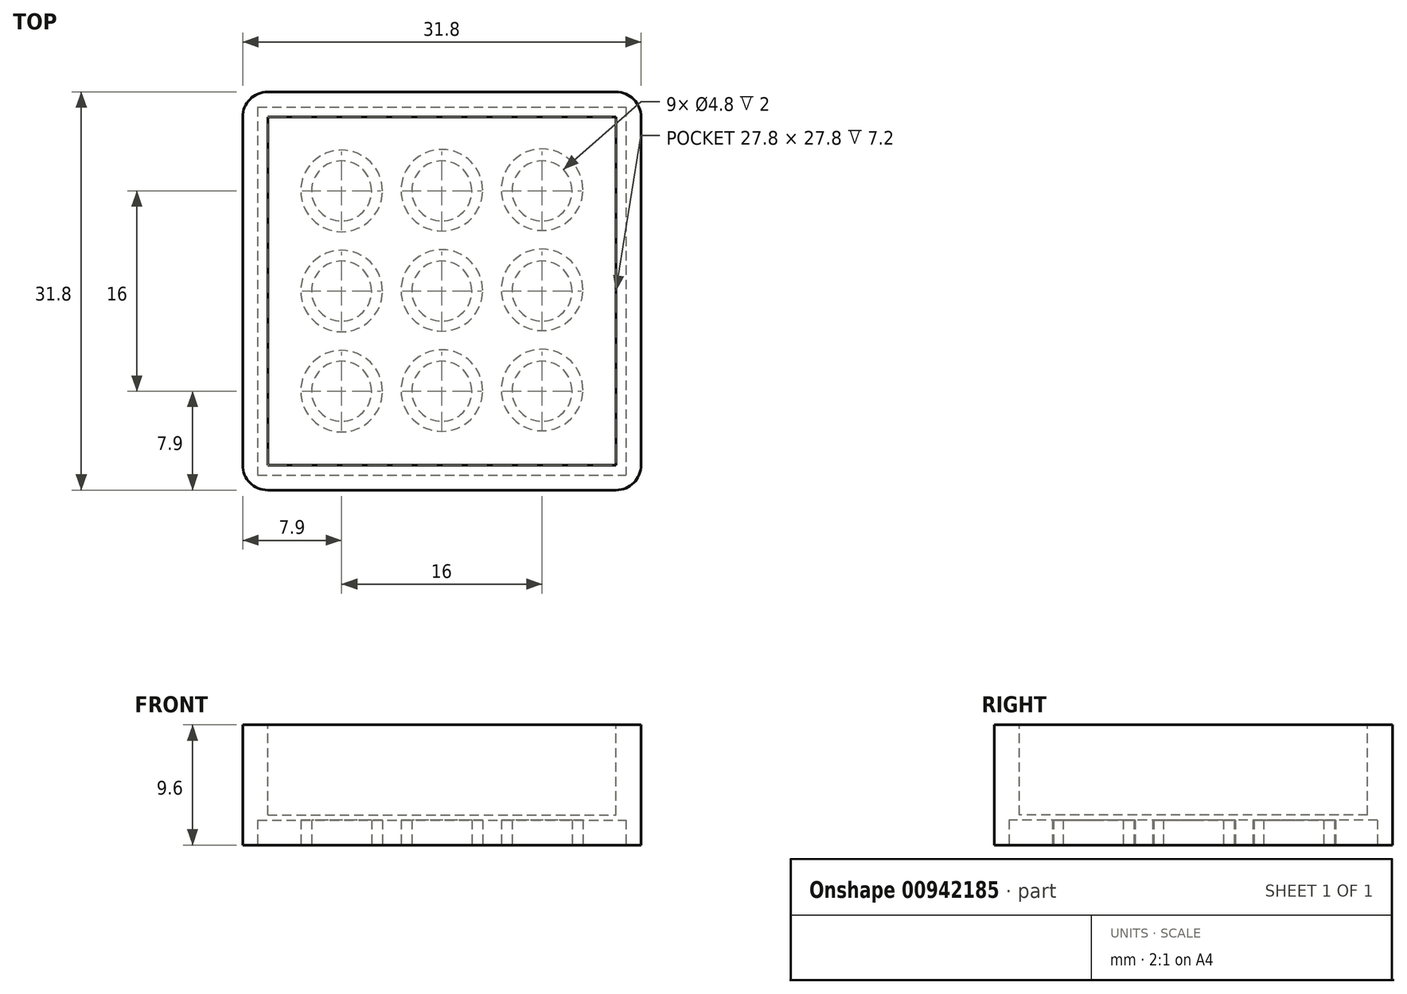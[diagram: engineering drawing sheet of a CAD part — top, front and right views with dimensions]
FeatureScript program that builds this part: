
annotation { "Feature Type Name" : "Feature", "Feature Type Description" : "" }
export const myFeature = defineFeature(function(context is Context, id is Id, definition is map)
    precondition{}
    {
        {
            var Q0;
            Q0=qCreatedBy(makeId("Top.planeOp"),FACE);
            var sketch = newSketch(context, id + "F0", { "sketchPlane" : qUnion([Q0])});
            skLineSegment(sketch, "E0.bottom", {"start": v(-15.9, 15.9) * mm, "end": v(15.9, 15.9) * mm});
            skLineSegment(sketch, "E0.top", {"start": v(-15.9, -15.9) * mm, "end": v(15.9, -15.9) * mm});
            skLineSegment(sketch, "E0.left", {"start": v(-15.9, 15.9) * mm, "end": v(-15.9, -15.9) * mm});
            skLineSegment(sketch, "E0.right", {"start": v(15.9, 15.9) * mm, "end": v(15.9, -15.9) * mm});
            skSolve(sketch);
        }
        {
            var Q0;
            Q0=qSketchRegion(id+"F0",true);
            extrude(context, id + "F1", {"entities" : qUnion([Q0]), "depth" : 9.6 * mm, "offsetDistance" : 25 * mm});
        }
        {
            var Q0;
            Q0=qCreatedBy(makeId("Top.planeOp"),FACE);
            var sketch = newSketch(context, id + "F2", { "sketchPlane" : qUnion([Q0])});
            skLineSegment(sketch, "E1.bottom", {"start": v(-14.7, 14.7) * mm, "end": v(14.7, 14.7) * mm});
            skLineSegment(sketch, "E1.top", {"start": v(-14.7, -14.7) * mm, "end": v(14.7, -14.7) * mm});
            skLineSegment(sketch, "E1.left", {"start": v(-14.7, 14.7) * mm, "end": v(-14.7, -14.7) * mm});
            skLineSegment(sketch, "E1.right", {"start": v(14.7, 14.7) * mm, "end": v(14.7, -14.7) * mm});
            skSolve(sketch);
        }
        {
            var Q0;
            Q0=qSketchRegion(id+"F2",true);
            extrude(context, id + "F3", {"entities" : qUnion([Q0]), "operationType" : NewBodyOperationType.REMOVE, "depth" : 2 * mm, "offsetDistance" : 25 * mm});
        }
        {
            var Q0;
            Q0=makeQuery(id+"F1.opExtrude","SWEPT_EDGE",EDGE,{"disambiguationData":[OSD([sQuery(id+"F0.wireOp",EDGE,"E0.top"),sQuery(id+"F0.wireOp",EDGE,"E0.left")])]});
            var Q1;
            Q1=makeQuery(id+"F1.opExtrude","SWEPT_EDGE",EDGE,{"disambiguationData":[OSD([sQuery(id+"F0.wireOp",EDGE,"E0.bottom"),sQuery(id+"F0.wireOp",EDGE,"E0.left")])]});
            var Q2;
            Q2=makeQuery(id+"F1.opExtrude","SWEPT_EDGE",EDGE,{"disambiguationData":[OSD([sQuery(id+"F0.wireOp",EDGE,"E0.bottom"),sQuery(id+"F0.wireOp",EDGE,"E0.right")])]});
            var Q3;
            Q3=makeQuery(id+"F1.opExtrude","SWEPT_EDGE",EDGE,{"disambiguationData":[OSD([sQuery(id+"F0.wireOp",EDGE,"E0.top"),sQuery(id+"F0.wireOp",EDGE,"E0.right")])]});
            fillet(context, id + "F4", {"entities" : qUnion([Q0, Q1, Q2, Q3]), "radius" : 2 * mm, "tangentPropagation" : true, "allowEdgeOverflow" : false});
        }
        {
            var Q0;
            Q0=qCreatedBy(makeId("Top.planeOp"),FACE);
            cPlane(context, id + "F5", {"entities" : qUnion([Q0]), "cplaneType" : CPlaneType.OFFSET, "offset" : 9.6 * mm, "width" : 150 * mm, "height" : 150 * mm});
        }
        {
            var Q0;
            Q0=qCreatedBy(id+"F5.planeOp",FACE);
            var sketch = newSketch(context, id + "F6", { "sketchPlane" : qUnion([Q0])});
            skLineSegment(sketch, "E2.bottom", {"start": v(-13.9, 13.9) * mm, "end": v(13.9, 13.9) * mm});
            skLineSegment(sketch, "E2.top", {"start": v(-13.9, -13.9) * mm, "end": v(13.9, -13.9) * mm});
            skLineSegment(sketch, "E2.left", {"start": v(-13.9, 13.9) * mm, "end": v(-13.9, -13.9) * mm});
            skLineSegment(sketch, "E2.right", {"start": v(13.9, 13.9) * mm, "end": v(13.9, -13.9) * mm});
            skPoint(sketch, "E2.middle", {"position": v(0, 0) * mm});
            skSolve(sketch);
        }
        {
            var Q0;
            Q0 = qSketchRegion(id + "F6", true);
            var Q1;
            Q1=sQuery(id+"F6.wireOp",EDGE,"2874aed3-c8fa-4ab8-97f8-e8d8516804c2.bottom");
            var Q2;
            Q2=sQuery(id+"F6.wireOp",EDGE,"2874aed3-c8fa-4ab8-97f8-e8d8516804c2.top");
            var Q3;
            Q3=sQuery(id+"F6.wireOp",EDGE,"2874aed3-c8fa-4ab8-97f8-e8d8516804c2.left");
            var Q4;
            Q4=sQuery(id+"F6.wireOp",EDGE,"2874aed3-c8fa-4ab8-97f8-e8d8516804c2.right");
            extrude(context, id + "F7", {"entities" : qUnion([Q0]), "operationType" : NewBodyOperationType.REMOVE, "surfaceEntities" : qUnion([Q1, Q2, Q3, Q4]), "oppositeDirection" : true, "depth" : 7.2 * mm, "offsetDistance" : 25 * mm});
        }
        {
            var Q0;
            Q0=qCreatedBy(makeId("Top.planeOp"),FACE);
            var sketch = newSketch(context, id + "F8", { "sketchPlane" : qUnion([Q0])});
            skCircle(sketch, "E3.1.1.0", {"center": v(-8, -8) * mm, "radius": 3.26 * mm});
            skCircle(sketch, "E4.0.1.0", {"center": v(-8, 0) * mm, "radius": 3.26 * mm});
            skCircle(sketch, "E4.0.2.0", {"center": v(-8, 8) * mm, "radius": 3.26 * mm});
            skCircle(sketch, "E4.1.0.0", {"center": v(0, -7.95) * mm, "radius": 3.26 * mm});
            skCircle(sketch, "E4.1.1.0", {"center": v(0, 0.05) * mm, "radius": 3.26 * mm});
            skCircle(sketch, "E4.1.2.0", {"center": v(0, 8.05) * mm, "radius": 3.26 * mm});
            skCircle(sketch, "E4.2.0.0", {"center": v(8, -7.9) * mm, "radius": 3.26 * mm});
            skCircle(sketch, "E4.2.1.0", {"center": v(8, 0.1) * mm, "radius": 3.26 * mm});
            skCircle(sketch, "E4.2.2.0", {"center": v(8, 8.1) * mm, "radius": 3.26 * mm});
            skLineSegment(sketch, "E4.direction1", {"start": v(-8, -8) * mm, "end": v(0, -7.95) * mm, "construction": true});
            skLineSegment(sketch, "E4.direction2", {"start": v(-8, -8) * mm, "end": v(-8, 0) * mm, "construction": true});
            skSolve(sketch);
        }
        {
            var Q0;
            Q0=qCreatedBy(makeId("Top.planeOp"),FACE);
            var sketch = newSketch(context, id + "F9", { "sketchPlane" : qUnion([Q0])});
            skCircle(sketch, "E5", {"center": v(-8, -8) * mm, "radius": 2.4 * mm});
            skCircle(sketch, "E6.0.1.0", {"center": v(-8, 0) * mm, "radius": 2.4 * mm});
            skCircle(sketch, "E6.0.2.0", {"center": v(-8, 8) * mm, "radius": 2.4 * mm});
            skCircle(sketch, "E6.1.0.0", {"center": v(0, -8) * mm, "radius": 2.4 * mm});
            skCircle(sketch, "E6.1.1.0", {"center": v(0, 0) * mm, "radius": 2.4 * mm});
            skCircle(sketch, "E6.1.2.0", {"center": v(0, 8) * mm, "radius": 2.4 * mm});
            skCircle(sketch, "E6.2.0.0", {"center": v(8, -8) * mm, "radius": 2.4 * mm});
            skCircle(sketch, "E6.2.1.0", {"center": v(8, 0) * mm, "radius": 2.4 * mm});
            skCircle(sketch, "E6.2.2.0", {"center": v(8, 8) * mm, "radius": 2.4 * mm});
            skLineSegment(sketch, "E6.direction1", {"start": v(-8, -8) * mm, "end": v(0, -8) * mm, "construction": true});
            skLineSegment(sketch, "E6.direction2", {"start": v(-8, -8) * mm, "end": v(-8, 0) * mm, "construction": true});
            skSolve(sketch);
        }
        {
            var Q0;
            Q0 = qSketchRegion(id + "F8", true);
            extrude(context, id + "F10", {"entities" : qUnion([Q0]), "operationType" : NewBodyOperationType.ADD, "depth" : 2.4 * mm, "offsetDistance" : 25 * mm});
        }
        {
            var Q0;
            Q0 = qSketchRegion(id + "F9", true);
            extrude(context, id + "F11", {"entities" : qUnion([Q0]), "operationType" : NewBodyOperationType.REMOVE, "depth" : 2 * mm, "offsetDistance" : 25 * mm});
        }
    });
